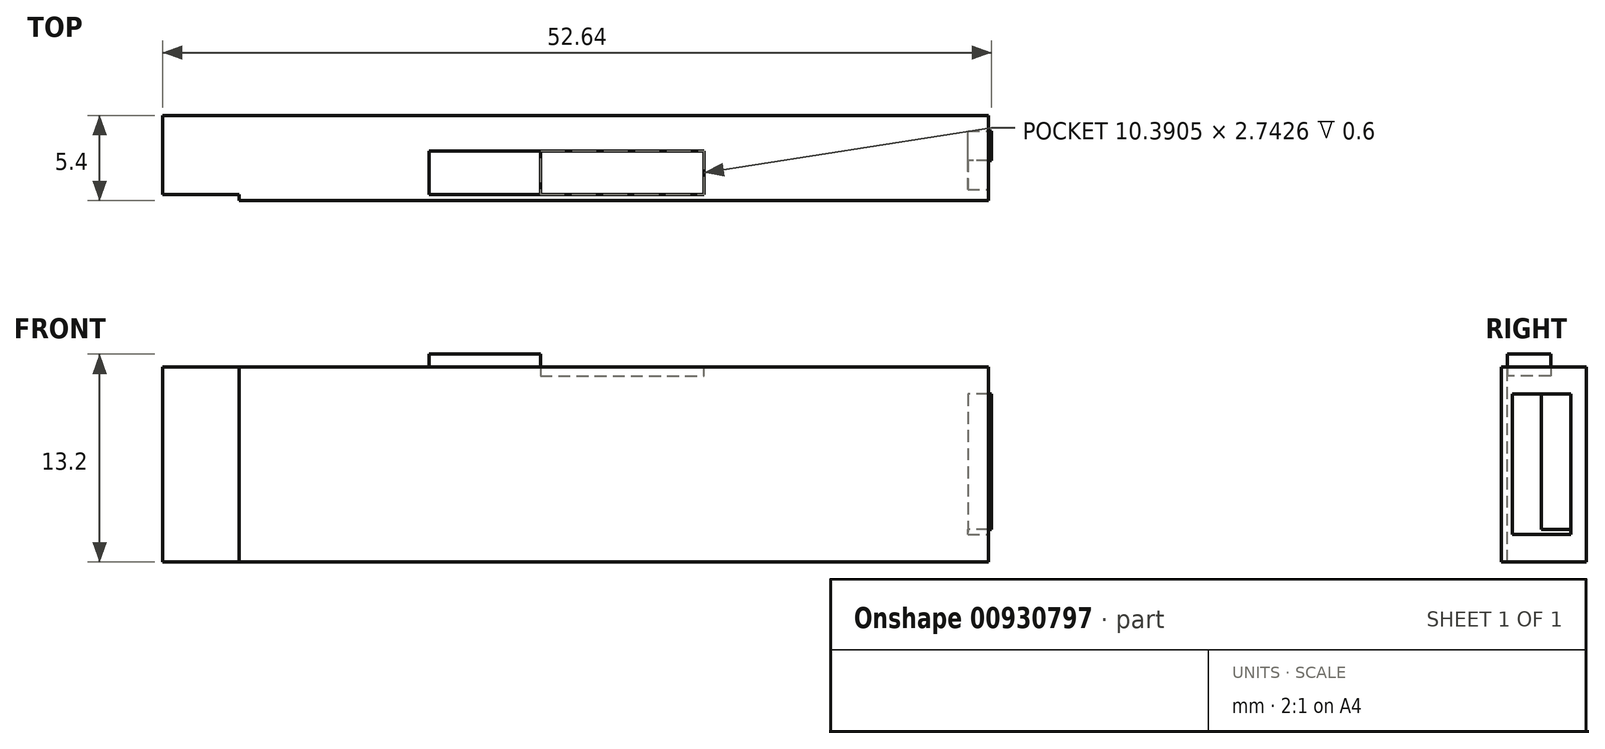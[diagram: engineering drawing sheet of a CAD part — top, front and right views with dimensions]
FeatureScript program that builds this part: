
annotation { "Feature Type Name" : "Feature", "Feature Type Description" : "" }
export const myFeature = defineFeature(function(context is Context, id is Id, definition is map)
    precondition{}
    {
        {
            var Q0;
            Q0=qCreatedBy(makeId("Front.planeOp"),FACE);
            var sketch = newSketch(context, id + "F0", { "sketchPlane" : qUnion([Q0])});
            skLineSegment(sketch, "E0", {"start": v(-22.68, 22.35) * mm, "end": v(29.76, 22.35) * mm});
            skLineSegment(sketch, "E1", {"start": v(29.76, 22.35) * mm, "end": v(29.76, 9.95) * mm});
            skLineSegment(sketch, "E2", {"start": v(29.76, 9.95) * mm, "end": v(-22.68, 9.95) * mm});
            skLineSegment(sketch, "E3", {"start": v(-22.68, 9.95) * mm, "end": v(-22.68, 22.35) * mm});
            skSolve(sketch);
        }
        {
            var Q0;
            Q0 = qSketchRegion(id + "F0", true);
            extrude(context, id + "F1", {"entities" : qUnion([Q0]), "depth" : 5 * mm, "offsetDistance" : 25 * mm});
        }
        {
            var Q0;
            Q0=makeQuery(id+"F1.opExtrude","CAP_FACE",FACE,{"disambiguationData":[OSD([sQuery(id+"F0.wireOp",EDGE,"E0"),sQuery(id+"F0.wireOp",EDGE,"E1"),sQuery(id+"F0.wireOp",EDGE,"E2"),sQuery(id+"F0.wireOp",EDGE,"E3")])],"isStart":false});
            var sketch = newSketch(context, id + "F2", { "sketchPlane" : qUnion([Q0])});
            skLineSegment(sketch, "E4", {"start": v(-17.8, 9.95) * mm, "end": v(-17.8, 22.35) * mm});
            skLineSegment(sketch, "E5", {"start": v(-17.8, 22.35) * mm, "end": v(29.76, 22.35) * mm});
            skLineSegment(sketch, "E6", {"start": v(29.76, 22.35) * mm, "end": v(29.76, 9.95) * mm});
            skLineSegment(sketch, "E7", {"start": v(29.76, 9.95) * mm, "end": v(-17.8, 9.95) * mm});
            skSolve(sketch);
        }
        {
            var Q0;
            Q0 = qSketchRegion(id + "F2", true);
            extrude(context, id + "F3", {"entities" : qUnion([Q0]), "operationType" : NewBodyOperationType.ADD, "depth" : 0.4 * mm, "offsetDistance" : 25 * mm});
        }
        {
            var Q0;
            Q0=makeQuery(id+"F3.boolean.opBoolean","MERGE",FACE,{"derivedFrom":[makeQuery(id+"F1.opExtrude","SWEPT_FACE",FACE,{"disambiguationData":[OSD([sQuery(id+"F0.wireOp",EDGE,"E0")])]}),makeQuery(id+"F3.opExtrude","SWEPT_FACE",FACE,{"disambiguationData":[OSD([sQuery(id+"F2.wireOp",EDGE,"E5")])]})]});
            var sketch = newSketch(context, id + "F4", { "sketchPlane" : qUnion([Q0])});
            skLineSegment(sketch, "E8", {"start": v(-5.75, -2.26) * mm, "end": v(11.7, -2.26) * mm});
            skLineSegment(sketch, "E9", {"start": v(11.7, -2.26) * mm, "end": v(11.7, -5) * mm});
            skLineSegment(sketch, "E10", {"start": v(11.7, -5) * mm, "end": v(-5.75, -5) * mm});
            skLineSegment(sketch, "E11", {"start": v(-5.75, -5) * mm, "end": v(-5.75, -2.26) * mm});
            skSolve(sketch);
        }
        {
            var Q0;
            Q0 = qSketchRegion(id + "F4", true);
            extrude(context, id + "F5", {"entities" : qUnion([Q0]), "operationType" : NewBodyOperationType.REMOVE, "oppositeDirection" : true, "depth" : 0.6 * mm, "offsetDistance" : 25 * mm});
        }
        {
            var Q0;
            Q0=makeQuery(id+"F5.boolean.opBoolean","COPY",FACE,{"derivedFrom":makeQuery(id+"F5.opExtrude","CAP_FACE",FACE,{"disambiguationData":[OSD([sQuery(id+"F4.wireOp",EDGE,"E8"),sQuery(id+"F4.wireOp",EDGE,"E9"),sQuery(id+"F4.wireOp",EDGE,"E10"),sQuery(id+"F4.wireOp",EDGE,"E11")])],"isStart":false})});
            var sketch = newSketch(context, id + "F6", { "sketchPlane" : qUnion([Q0])});
            skLineSegment(sketch, "E12", {"start": v(-5.75, -2.26) * mm, "end": v(1.3, -2.26) * mm});
            skLineSegment(sketch, "E13", {"start": v(1.3, -2.26) * mm, "end": v(1.3, -5) * mm});
            skLineSegment(sketch, "E14", {"start": v(1.3, -5) * mm, "end": v(-5.75, -5) * mm});
            skLineSegment(sketch, "E15", {"start": v(-5.75, -5) * mm, "end": v(-5.75, -2.26) * mm});
            skSolve(sketch);
        }
        {
            var Q0;
            Q0 = qSketchRegion(id + "F6", true);
            extrude(context, id + "F7", {"entities" : qUnion([Q0]), "operationType" : NewBodyOperationType.ADD, "depth" : 1.4 * mm, "offsetDistance" : 25 * mm});
        }
        {
            var Q0;
            Q0=makeQuery(id+"F3.boolean.opBoolean","MERGE",FACE,{"derivedFrom":[makeQuery(id+"F1.opExtrude","SWEPT_FACE",FACE,{"disambiguationData":[OSD([sQuery(id+"F0.wireOp",EDGE,"E1")])]}),makeQuery(id+"F3.opExtrude","SWEPT_FACE",FACE,{"disambiguationData":[OSD([sQuery(id+"F2.wireOp",EDGE,"E6")])]})]});
            var sketch = newSketch(context, id + "F8", { "sketchPlane" : qUnion([Q0])});
            skLineSegment(sketch, "E16", {"start": v(-4.7, 20.62) * mm, "end": v(-4.7, 11.68) * mm});
            skLineSegment(sketch, "E17", {"start": v(-4.7, 11.68) * mm, "end": v(-0.98, 11.68) * mm});
            skLineSegment(sketch, "E18", {"start": v(-0.98, 11.68) * mm, "end": v(-0.98, 20.62) * mm});
            skLineSegment(sketch, "E19", {"start": v(-0.98, 20.62) * mm, "end": v(-4.7, 20.62) * mm});
            skSolve(sketch);
        }
        {
            var Q0;
            Q0 = qSketchRegion(id + "F8", true);
            extrude(context, id + "F9", {"entities" : qUnion([Q0]), "operationType" : NewBodyOperationType.REMOVE, "oppositeDirection" : true, "depth" : 1.3 * mm, "offsetDistance" : 25 * mm});
        }
        {
            var Q0;
            Q0=makeQuery(id+"F9.boolean.opBoolean","COPY",FACE,{"derivedFrom":makeQuery(id+"F9.opExtrude","CAP_FACE",FACE,{"disambiguationData":[OSD([sQuery(id+"F8.wireOp",EDGE,"E16"),sQuery(id+"F8.wireOp",EDGE,"E17"),sQuery(id+"F8.wireOp",EDGE,"E18"),sQuery(id+"F8.wireOp",EDGE,"E19")])],"isStart":false})});
            var sketch = newSketch(context, id + "F10", { "sketchPlane" : qUnion([Q0])});
            skLineSegment(sketch, "E20", {"start": v(-2.84, 20.62) * mm, "end": v(-0.98, 20.62) * mm});
            skLineSegment(sketch, "E21", {"start": v(-0.98, 20.62) * mm, "end": v(-0.98, 11.68) * mm});
            skLineSegment(sketch, "E22", {"start": v(-2.84, 20.62) * mm, "end": v(-2.84, 12.01) * mm});
            skLineSegment(sketch, "E23", {"start": v(-2.84, 12.01) * mm, "end": v(-0.98, 12.01) * mm});
            skSolve(sketch);
        }
        {
            var Q0;
            Q0 = qSketchRegion(id + "F10", true);
            extrude(context, id + "F11", {"entities" : qUnion([Q0]), "operationType" : NewBodyOperationType.ADD, "depth" : 1.5 * mm, "offsetDistance" : 25 * mm});
        }
    });
